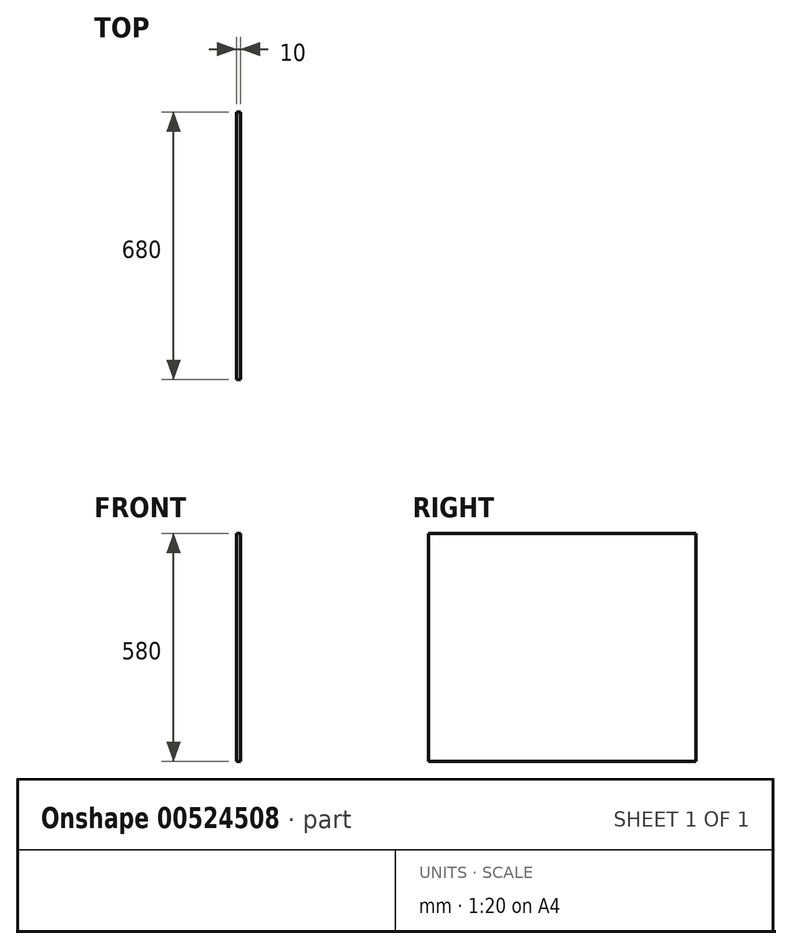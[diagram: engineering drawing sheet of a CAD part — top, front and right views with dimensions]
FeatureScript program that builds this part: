
annotation { "Feature Type Name" : "Feature", "Feature Type Description" : "" }
export const myFeature = defineFeature(function(context is Context, id is Id, definition is map)
    precondition{}
    {
        {
            var Q0;
            Q0=qCreatedBy(makeId("Right.planeOp"),FACE);
            var sketch = newSketch(context, id + "F0", { "sketchPlane" : qUnion([Q0])});
            skLineSegment(sketch, "E0.bottom", {"start": v(-340, -290) * mm, "end": v(340, -290) * mm});
            skLineSegment(sketch, "E0.top", {"start": v(-340, 290) * mm, "end": v(340, 290) * mm});
            skLineSegment(sketch, "E0.left", {"start": v(-340, -290) * mm, "end": v(-340, 290) * mm});
            skLineSegment(sketch, "E0.right", {"start": v(340, -290) * mm, "end": v(340, 290) * mm});
            skPoint(sketch, "E0.middle", {"position": v(0, 0) * mm});
            skSolve(sketch);
        }
        {
            var Q0;
            Q0=makeQuery(id+"F0.imprint","IMPRINT",FACE,{"disambiguationData":[TD([[makeQuery(id+"F0.imprint","IMPRINT",EDGE,{"derivedFrom":sQuery(id+"F0.wireOp",EDGE,"E0.bottom")}),1.0]])]});
            extrude(context, id + "F1", {"entities" : qUnion([Q0]), "depth" : 10 * mm, "offsetDistance" : 25 * mm});
        }
    });
